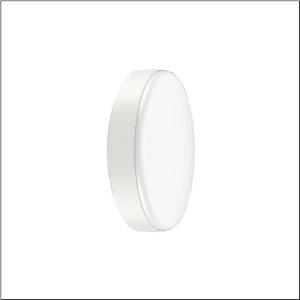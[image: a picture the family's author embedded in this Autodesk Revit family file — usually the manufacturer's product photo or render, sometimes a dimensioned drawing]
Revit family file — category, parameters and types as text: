
# Revit family: round_31_51wc10mb34as
name_source: partatom
category: Lighting Fixtures
units: mm (PartAtom-declared; Revit-internal decimal feet)

## family parameters
Cut with Voids When Loaded = No
Host = Face
Light Source = No
Part Type = Normal
Room Calculation Point = No
Round Connector Dimension = Use Diameter
Shared = No

## types (1)
- --- (1 x LED, 4250 lm, 35.4 W, 3000K)
    Apparent Load = 35 VA
    CIE Flux Codes = 44 75 94 94 100
    Color Rendering = 80
    Color Temperature = 3000K
    Default Elevation = 1800 mm
    Description = Round 31, wall and ceiling luminaire, primary optical cover: cover, of PC, opal, light emission: direct distribution, primary light characteristic: symmetric, installation type: surface-mounted, LED, rated luminous flux: 4.250lm, luminous efficacy: 120lm/W, light colour: 830, colour temperature: 3000K, control gear: ON/OFF Multilumen, with terminal, 3-pole, max. 2.5mm², mains connection: 220..240V, AC, 50/60Hz, rated input power: 35W, luminaire housing, of PC, traffic white (RAL 9016), diameter: 480mm, brightness and presence sensor, HF sensor, protection rating (complete): IP65, insulation class (complete): insulation class II (safety insulation), certification: CE, impact resistance: IK10, permissible operating ambient temperature: -20..+40°C, permissible storage temperature: -20..+60°C, packaging unit: 1 piece
    Height = 97 mm
    Lamp = 1 x LED
    Lamp Light Flux = 4250 lm
    Lamp Power = 35.4 W
    Lamp count = 1
    Length = 480 mm
    Luminous efficacy = 120 lm/W
    Manufacturer = Siteco
    ModVariant = No
    Model = 51WC10MB34AS
    Mounting Place = Wall
    Mounting Type = Surface mounted
    Number of Poles = 1
    OnlyDefault = Yes
    Power Factor = 1
    Product Name = Round 31
    Product group = wall and ceiling luminaire
    ProductGroupID = 2001
    Protection Class = Protection class II
    Protection Degree = IP 65
    RLX_Detail_Level = 1
    RLX_Emergency_Light_Flux = 0 lm
    RLX_Emergency_Type = 0
    RLX_Emergency_Type_DB = No
    RlxData = <blob elided: 41381 chars, md5=31748a89>
    Socket = socket
    Standby Power = 0 W
    System Light Flux = 4250 lm
    System Power = 35 W
    Type Comments = factory setting: luminous flux: 100 % | (ON | ON)
    Type Image = l_1007188.jpg
    URL = http://relux.com
    VarID = @adj_115755
    Voltage = 0 V
    Weight = 0.00 kg
    Width = 0 mm  [stored 0 ft]

note: [stored X ft] marks values corroborated as IEEE doubles in the binary element streams (Revit-internal decimal feet)

## geometry (parser evidence)
native form markers: Blend x4, Sweep x12
no freeform markers — native parametric forms only
